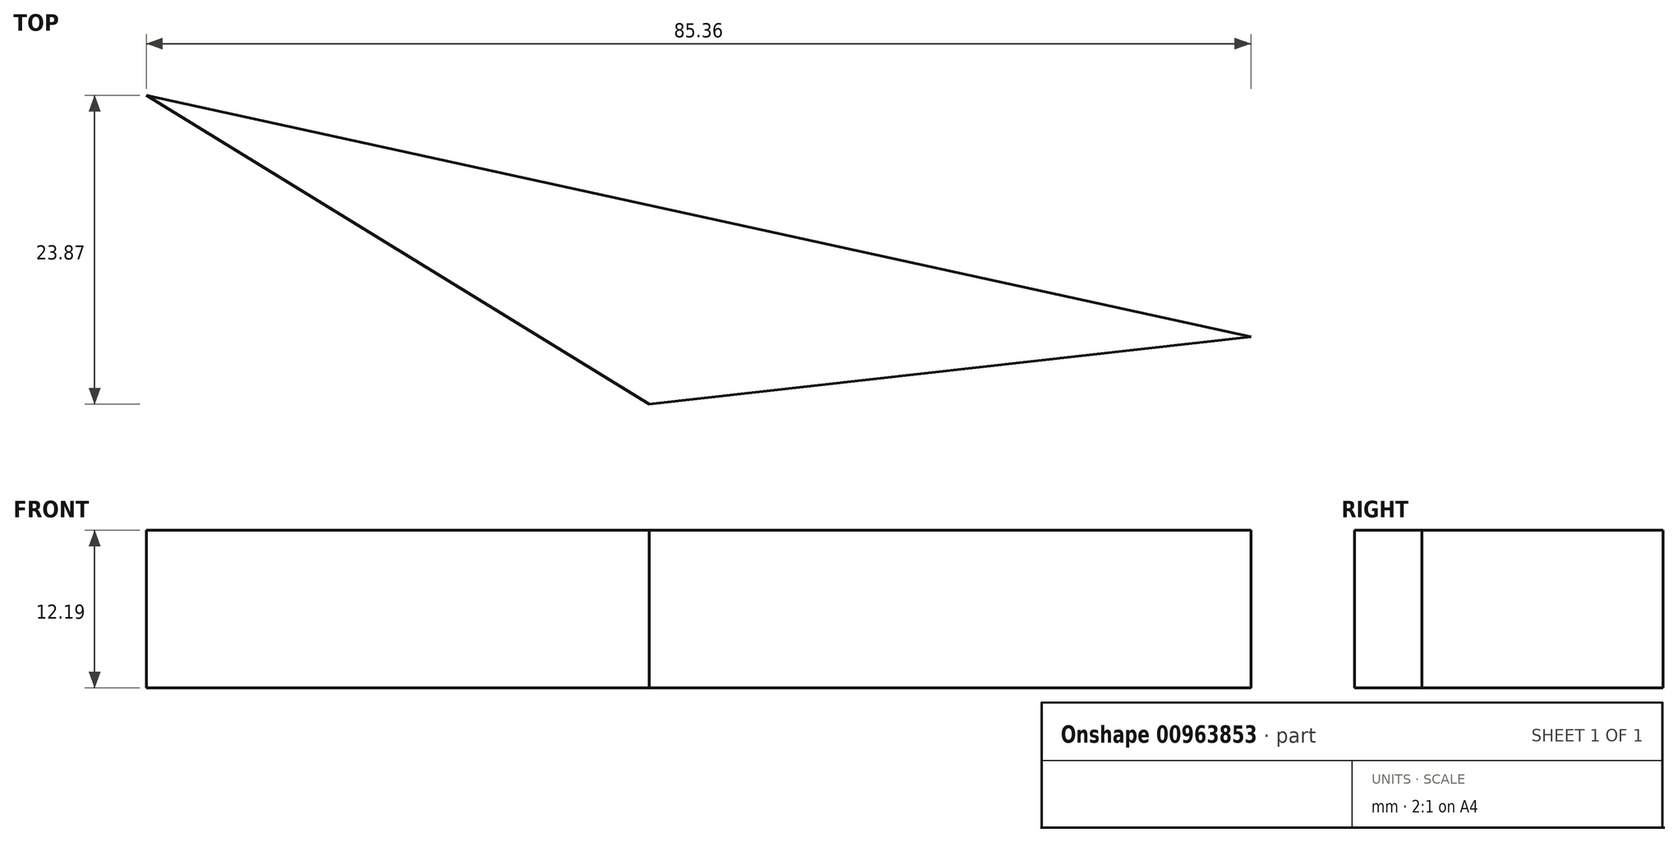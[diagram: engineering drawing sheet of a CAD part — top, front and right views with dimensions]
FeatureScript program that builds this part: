
annotation { "Feature Type Name" : "Feature", "Feature Type Description" : "" }
export const myFeature = defineFeature(function(context is Context, id is Id, definition is map)
    precondition{}
    {
        {
            var Q0;
            Q0=qCreatedBy(makeId("Top.planeOp"),FACE);
            var sketch = newSketch(context, id + "F0", { "sketchPlane" : qUnion([Q0])});
            skLineSegment(sketch, "E0", {"start": v(-49.26, 37.94) * mm, "end": v(-10.4, 14.07) * mm});
            skLineSegment(sketch, "E1", {"start": v(-10.4, 14.07) * mm, "end": v(36.1, 19.28) * mm});
            skLineSegment(sketch, "E2", {"start": v(36.1, 19.28) * mm, "end": v(-49.26, 37.94) * mm});
            skSolve(sketch);
        }
        {
            var Q0;
            Q0=makeQuery(id+"F0.imprint","IMPRINT",FACE,{"disambiguationData":[TD([[makeQuery(id+"F0.imprint","IMPRINT",EDGE,{"derivedFrom":sQuery(id+"F0.wireOp",EDGE,"E0")}),1.0]])]});
            extrude(context, id + "F1", {"entities" : qUnion([Q0]), "depth" : 12.2 * mm, "offsetDistance" : 25.4 * mm});
        }
    });
